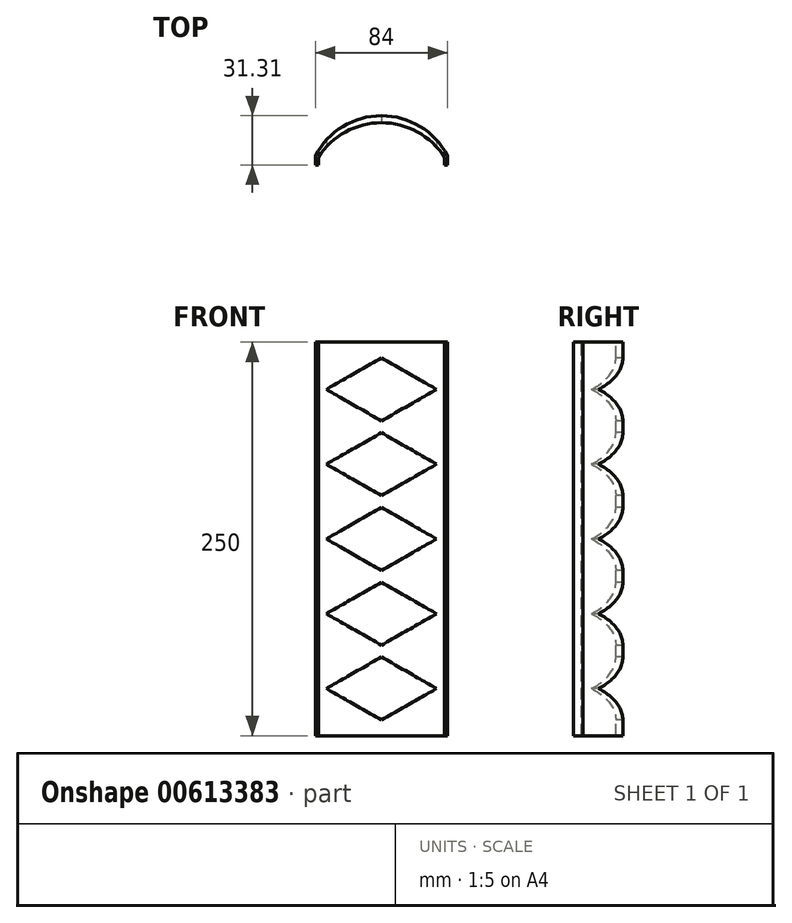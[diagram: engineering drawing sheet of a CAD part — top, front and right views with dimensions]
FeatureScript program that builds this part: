
annotation { "Feature Type Name" : "Feature", "Feature Type Description" : "" }
export const myFeature = defineFeature(function(context is Context, id is Id, definition is map)
    precondition{}
    {
        {
            var Q0;
            Q0=qCreatedBy(makeId("Top.planeOp"),FACE);
            var sketch = newSketch(context, id + "F0", { "sketchPlane" : qUnion([Q0])});
            skCircle(sketch, "E0", {"center": v(0, 0) * mm, "radius": 47.5 * mm});
            skLineSegment(sketch, "E1", {"start": v(-42, 22.19) * mm, "end": v(-42, 16.19) * mm});
            skLineSegment(sketch, "E2", {"start": v(-42, 16.19) * mm, "end": v(42, 16.19) * mm});
            skLineSegment(sketch, "E3", {"start": v(42, 16.19) * mm, "end": v(42, 22.19) * mm});
            skSolve(sketch);
        }
        {
            var Q0;
            {var subQ0=sQuery(id+"F0.wireOp",EDGE,"E1");Q0=makeQuery(id+"F0.imprint","IMPRINT",FACE,{"disambiguationData":[TD([[makeQuery(id+"F0.imprint","IMPRINT",EDGE,{"derivedFrom":subQ0}),1.0]])]});}
            extrude(context, id + "F1", {"entities" : qUnion([Q0]), "depth" : 250 * mm, "offsetDistance" : 25 * mm});
        }
        {
            var Q0;
            Q0=makeQuery(id+"F1.opExtrude","CAP_FACE",FACE,{"disambiguationData":[OSD([sQuery(id+"F0.wireOp",EDGE,"E0"),sQuery(id+"F0.wireOp",EDGE,"E1"),sQuery(id+"F0.wireOp",EDGE,"E2"),sQuery(id+"F0.wireOp",EDGE,"E3")])],"isStart":false});
            var sketch = newSketch(context, id + "F2", { "sketchPlane" : qUnion([Q0])});
            skLineSegment(sketch, "E4", {"start": v(-40, 21.19) * mm, "end": v(-40, 16.19) * mm});
            skLineSegment(sketch, "E5", {"start": v(-40, 16.19) * mm, "end": v(40, 16.19) * mm});
            skLineSegment(sketch, "E6", {"start": v(40, 16.19) * mm, "end": v(40, 21.19) * mm});
            skCircle(sketch, "E7", {"center": v(0, -4.43) * mm, "radius": 47.5 * mm});
            skSolve(sketch);
        }
        {
            var Q0;
            {var subQ0=sQuery(id+"F2.wireOp",EDGE,"E4");Q0=makeQuery(id+"F2.imprint","IMPRINT",FACE,{"disambiguationData":[TD([[makeQuery(id+"F2.imprint","IMPRINT",EDGE,{"derivedFrom":subQ0}),1.0]])]});}
            extrude(context, id + "F3", {"entities" : qUnion([Q0]), "operationType" : NewBodyOperationType.REMOVE, "endBound" : BoundingType.THROUGH_ALL, "oppositeDirection" : true, "depth" : 25 * mm, "offsetDistance" : 25 * mm});
        }
        {
            var Q0;
            Q0=qCreatedBy(makeId("Front.planeOp"),FACE);
            var sketch = newSketch(context, id + "F4", { "sketchPlane" : qUnion([Q0])});
            skLineSegment(sketch, "E8", {"start": v(0, 240) * mm, "end": v(-35, 220) * mm});
            skLineSegment(sketch, "E9", {"start": v(-35, 220) * mm, "end": v(0, 200) * mm});
            skLineSegment(sketch, "E10", {"start": v(0, 200) * mm, "end": v(35, 220) * mm});
            skLineSegment(sketch, "E11", {"start": v(35, 220) * mm, "end": v(0, 240) * mm});
            skLineSegment(sketch, "E12", {"start": v(0, 192.5) * mm, "end": v(-35, 172.5) * mm});
            skLineSegment(sketch, "E13", {"start": v(-35, 172.5) * mm, "end": v(0, 152.5) * mm});
            skLineSegment(sketch, "E14", {"start": v(0, 152.5) * mm, "end": v(35, 172.5) * mm});
            skLineSegment(sketch, "E15", {"start": v(35, 172.5) * mm, "end": v(0, 192.5) * mm});
            skLineSegment(sketch, "E16", {"start": v(0, 145) * mm, "end": v(-35, 125) * mm});
            skLineSegment(sketch, "E17", {"start": v(-35, 125) * mm, "end": v(0, 105) * mm});
            skLineSegment(sketch, "E18", {"start": v(0, 105) * mm, "end": v(35, 125) * mm});
            skLineSegment(sketch, "E19", {"start": v(35, 125) * mm, "end": v(0, 145) * mm});
            skLineSegment(sketch, "E20", {"start": v(0, 97.5) * mm, "end": v(-35, 77.5) * mm});
            skLineSegment(sketch, "E21", {"start": v(-35, 77.5) * mm, "end": v(0, 57.5) * mm});
            skLineSegment(sketch, "E22", {"start": v(0, 57.5) * mm, "end": v(35, 77.5) * mm});
            skLineSegment(sketch, "E23", {"start": v(35, 77.5) * mm, "end": v(0, 97.5) * mm});
            skLineSegment(sketch, "E24", {"start": v(0, 50) * mm, "end": v(-35, 30) * mm});
            skLineSegment(sketch, "E25", {"start": v(-35, 30) * mm, "end": v(0, 10) * mm});
            skLineSegment(sketch, "E26", {"start": v(0, 10) * mm, "end": v(35, 30) * mm});
            skLineSegment(sketch, "E27", {"start": v(35, 30) * mm, "end": v(0, 50) * mm});
            skSolve(sketch);
        }
        {
            var Q0;
            Q0 = qSketchRegion(id + "F4", true);
            extrude(context, id + "F5", {"entities" : qUnion([Q0]), "operationType" : NewBodyOperationType.REMOVE, "endBound" : BoundingType.THROUGH_ALL, "oppositeDirection" : true, "depth" : 25 * mm, "offsetDistance" : 25 * mm});
        }
    });
